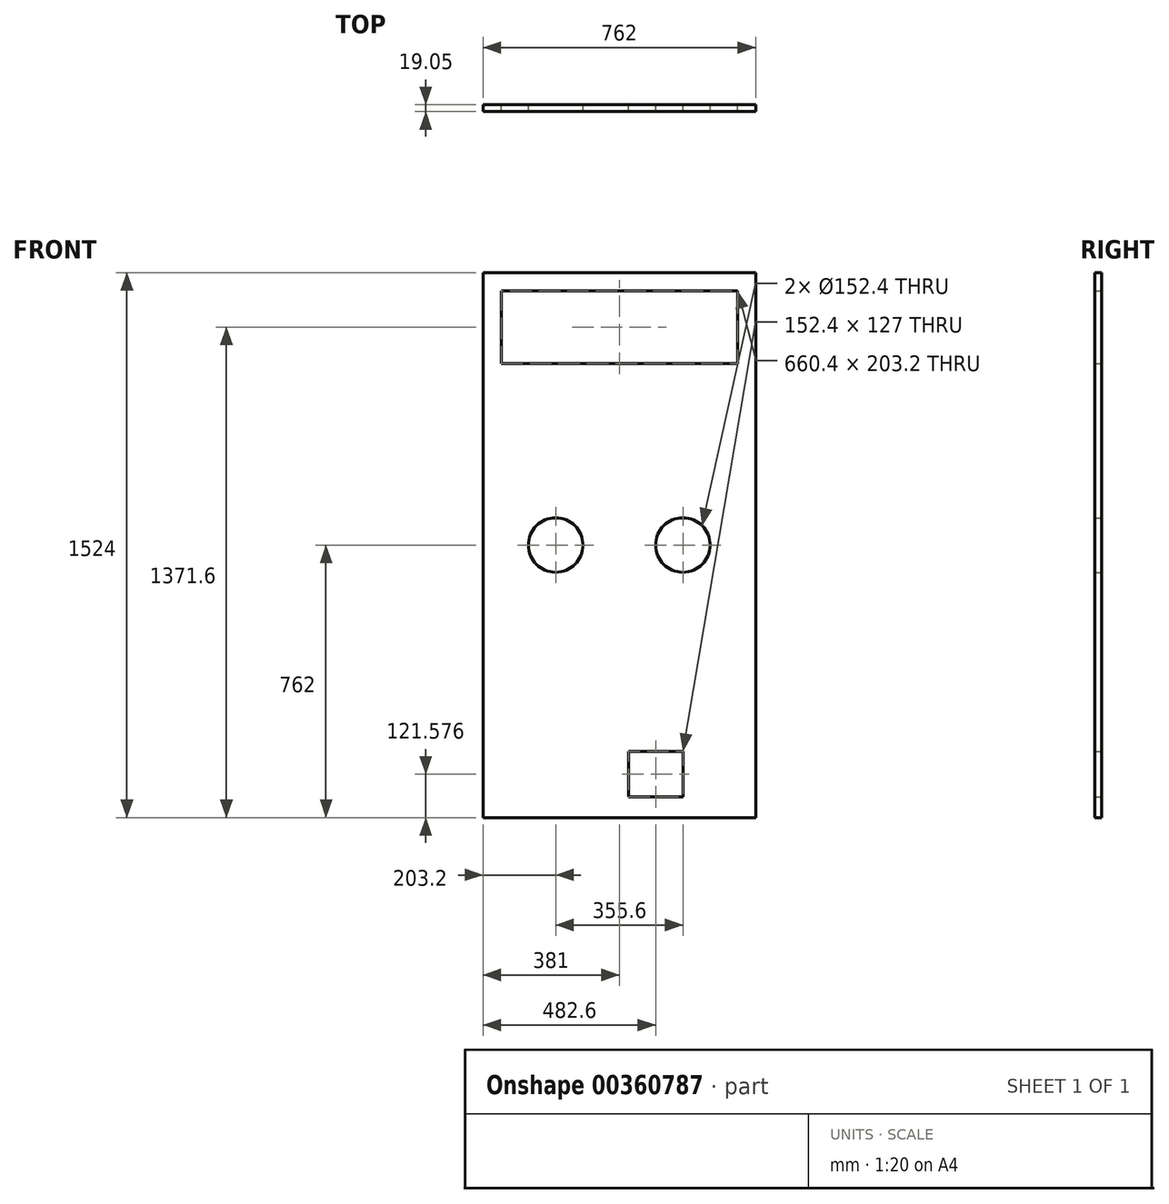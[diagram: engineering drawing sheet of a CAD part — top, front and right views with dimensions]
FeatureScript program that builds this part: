
annotation { "Feature Type Name" : "Feature", "Feature Type Description" : "" }
export const myFeature = defineFeature(function(context is Context, id is Id, definition is map)
    precondition{}
    {
        {
            var Q0;
            Q0=qCreatedBy(makeId("Front.planeOp"),FACE);
            var sketch = newSketch(context, id + "F0", { "sketchPlane" : qUnion([Q0])});
            skLineSegment(sketch, "E0.bottom", {"start": v(0, 0) * mm, "end": v(762, 0) * mm});
            skLineSegment(sketch, "E0.top", {"start": v(0, 1524) * mm, "end": v(762, 1524) * mm});
            skLineSegment(sketch, "E0.left", {"start": v(0, 0) * mm, "end": v(0, 1524) * mm});
            skLineSegment(sketch, "E0.right", {"start": v(762, 0) * mm, "end": v(762, 1524) * mm});
            skCircle(sketch, "E1", {"center": v(203.2, 762) * mm, "radius": 76.2 * mm});
            skCircle(sketch, "E2", {"center": v(558.8, 762) * mm, "radius": 76.2 * mm});
            skLineSegment(sketch, "E3.bottom", {"start": v(406.4, 185.08) * mm, "end": v(558.8, 185.08) * mm});
            skLineSegment(sketch, "E3.top", {"start": v(406.4, 58.08) * mm, "end": v(558.8, 58.08) * mm});
            skLineSegment(sketch, "E3.left", {"start": v(406.4, 185.08) * mm, "end": v(406.4, 58.08) * mm});
            skLineSegment(sketch, "E3.right", {"start": v(558.8, 185.08) * mm, "end": v(558.8, 58.08) * mm});
            skLineSegment(sketch, "E4.bottom", {"start": v(50.8, 1473.2) * mm, "end": v(711.2, 1473.2) * mm});
            skLineSegment(sketch, "E4.top", {"start": v(50.8, 1270) * mm, "end": v(711.2, 1270) * mm});
            skLineSegment(sketch, "E4.left", {"start": v(50.8, 1473.2) * mm, "end": v(50.8, 1270) * mm});
            skLineSegment(sketch, "E4.right", {"start": v(711.2, 1473.2) * mm, "end": v(711.2, 1270) * mm});
            skSolve(sketch);
        }
        {
            var Q0;
            Q0=makeQuery(id+"F0.imprint","IMPRINT",FACE,{"disambiguationData":[TD([[makeQuery(id+"F0.imprint","IMPRINT",EDGE,{"derivedFrom":sQuery(id+"F0.wireOp",EDGE,"E0.bottom")}),1.0]])]});
            extrude(context, id + "F1", {"entities" : qUnion([Q0]), "depth" : 19.05 * mm});
        }
    });
